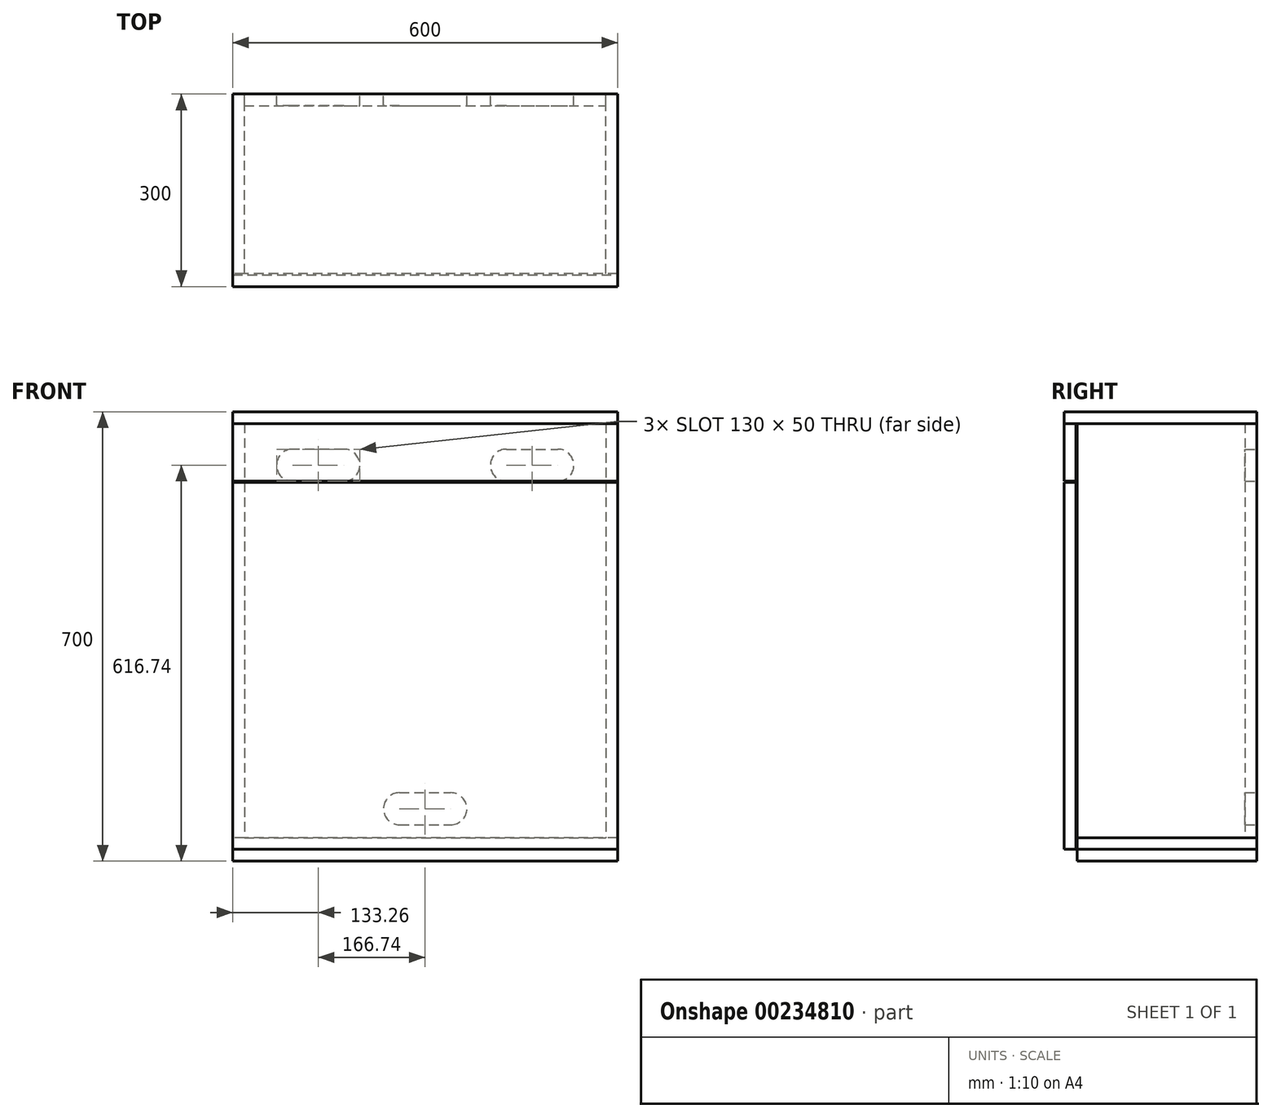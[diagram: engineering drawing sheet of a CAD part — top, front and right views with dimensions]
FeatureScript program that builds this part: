
annotation { "Feature Type Name" : "Feature", "Feature Type Description" : "" }
export const myFeature = defineFeature(function(context is Context, id is Id, definition is map)
    precondition{}
    {
        {
            var Q0;
            Q0=qCreatedBy(makeId("Top.planeOp"),FACE);
            var sketch = newSketch(context, id + "F0", { "sketchPlane" : qUnion([Q0])});
            skLineSegment(sketch, "E0.bottom", {"start": v(300, 139.87) * mm, "end": v(-300, 139.87) * mm});
            skLineSegment(sketch, "E0.top", {"start": v(300, -139.87) * mm, "end": v(-300, -139.87) * mm});
            skLineSegment(sketch, "E0.left", {"start": v(300, 139.87) * mm, "end": v(300, -139.87) * mm});
            skLineSegment(sketch, "E0.right", {"start": v(-300, 139.87) * mm, "end": v(-300, -139.87) * mm});
            skPoint(sketch, "E0.middle", {"position": v(0, 0) * mm});
            skSolve(sketch);
        }
        {
            var Q0;
            Q0=makeQuery(id+"F0.imprint","IMPRINT",FACE,{"disambiguationData":[TD([[makeQuery(id+"F0.imprint","IMPRINT",EDGE,{"derivedFrom":sQuery(id+"F0.wireOp",EDGE,"E0.bottom")}),1.0]])]});
            extrude(context, id + "F1", {"entities" : qUnion([Q0]), "depth" : 18.26 * mm, "offsetDistance" : 25 * mm});
        }
        {
            var Q0;
            Q0=makeQuery(id+"F1.opExtrude","CAP_FACE",FACE,{"disambiguationData":[OSD([sQuery(id+"F0.wireOp",EDGE,"E0.bottom"),sQuery(id+"F0.wireOp",EDGE,"E0.top"),sQuery(id+"F0.wireOp",EDGE,"E0.left"),sQuery(id+"F0.wireOp",EDGE,"E0.right")])],"isStart":false});
            var sketch = newSketch(context, id + "F2", { "sketchPlane" : qUnion([Q0])});
            skLineSegment(sketch, "E1.bottom", {"start": v(-300, -139.87) * mm, "end": v(-281.74, -139.87) * mm});
            skLineSegment(sketch, "E1.top", {"start": v(-300, 139.87) * mm, "end": v(-281.74, 139.87) * mm});
            skLineSegment(sketch, "E1.left", {"start": v(-300, -139.87) * mm, "end": v(-300, 139.87) * mm});
            skLineSegment(sketch, "E1.right", {"start": v(-281.74, -139.87) * mm, "end": v(-281.74, 139.87) * mm});
            skLineSegment(sketch, "E2.bottom", {"start": v(300, -139.87) * mm, "end": v(281.74, -139.87) * mm});
            skLineSegment(sketch, "E2.top", {"start": v(300, 139.87) * mm, "end": v(281.74, 139.87) * mm});
            skLineSegment(sketch, "E2.left", {"start": v(300, -139.87) * mm, "end": v(300, 139.87) * mm});
            skLineSegment(sketch, "E2.right", {"start": v(281.74, -139.87) * mm, "end": v(281.74, 139.87) * mm});
            skLineSegment(sketch, "E3.bottom", {"start": v(-281.74, 139.87) * mm, "end": v(281.74, 139.87) * mm});
            skLineSegment(sketch, "E3.top", {"start": v(-281.74, 121.61) * mm, "end": v(281.74, 121.61) * mm});
            skLineSegment(sketch, "E3.left", {"start": v(-281.74, 139.87) * mm, "end": v(-281.74, 121.61) * mm});
            skLineSegment(sketch, "E3.right", {"start": v(281.74, 139.87) * mm, "end": v(281.74, 121.61) * mm});
            skSolve(sketch);
        }
        {
            var Q0;
            Q0=makeQuery(id+"F2.imprint","IMPRINT",FACE,{"disambiguationData":[TD([[makeQuery(id+"F2.imprint","IMPRINT",EDGE,{"derivedFrom":sQuery(id+"F2.wireOp",EDGE,"E2.bottom")}),-1.0]])]});
            extrude(context, id + "F3", {"entities" : qUnion([Q0]), "depth" : 645.22 * mm, "offsetDistance" : 25 * mm});
        }
        {
            var Q0;
            Q0=makeQuery(id+"F2.imprint","IMPRINT",FACE,{"disambiguationData":[TD([[makeQuery(id+"F2.imprint","IMPRINT",EDGE,{"derivedFrom":sQuery(id+"F2.wireOp",EDGE,"E3.bottom")}),1.0]])]});
            var Q1;
            Q1=makeQuery(id+"F3.opExtrude","CAP_FACE",FACE,{"disambiguationData":[OSD([sQuery(id+"F2.wireOp",EDGE,"E2.bottom"),sQuery(id+"F2.wireOp",EDGE,"E2.top"),sQuery(id+"F2.wireOp",EDGE,"E2.left"),sQuery(id+"F2.wireOp",EDGE,"E2.right"),sQuery(id+"F2.wireOp",EDGE,"E3.right")])],"isStart":false});
            extrude(context, id + "F4", {"entities" : qUnion([Q0]), "endBound" : BoundingType.UP_TO_SURFACE, "endBoundEntityFace" : qUnion([Q1]), "depth" : 25 * mm});
        }
        {
            var Q0;
            Q0=makeQuery(id+"F2.imprint","IMPRINT",FACE,{"disambiguationData":[TD([[makeQuery(id+"F2.imprint","IMPRINT",EDGE,{"derivedFrom":sQuery(id+"F2.wireOp",EDGE,"E1.bottom")}),-1.0]])]});
            var Q1;
            Q1=makeQuery(id+"F4.opExtrude","CAP_FACE",FACE,{"disambiguationData":[OSD([sQuery(id+"F2.wireOp",EDGE,"E3.bottom"),sQuery(id+"F2.wireOp",EDGE,"E3.top"),sQuery(id+"F2.wireOp",EDGE,"E3.left"),sQuery(id+"F2.wireOp",EDGE,"E3.right")])],"isStart":false});
            extrude(context, id + "F5", {"entities" : qUnion([Q0]), "endBound" : BoundingType.UP_TO_SURFACE, "endBoundEntityFace" : qUnion([Q1]), "depth" : 25 * mm});
        }
        {
            var Q0;
            Q0=makeQuery(id+"F5.opExtrude","CAP_FACE",FACE,{"disambiguationData":[OSD([sQuery(id+"F2.wireOp",EDGE,"E1.bottom"),sQuery(id+"F2.wireOp",EDGE,"E1.top"),sQuery(id+"F2.wireOp",EDGE,"E1.left"),sQuery(id+"F2.wireOp",EDGE,"E1.right"),sQuery(id+"F2.wireOp",EDGE,"E3.left")])],"isStart":false});
            var sketch = newSketch(context, id + "F6", { "sketchPlane" : qUnion([Q0])});
            skLineSegment(sketch, "E4.bottom", {"start": v(-300, 139.87) * mm, "end": v(300, 139.87) * mm});
            skLineSegment(sketch, "E4.top", {"start": v(-300, -160.13) * mm, "end": v(300, -160.13) * mm});
            skLineSegment(sketch, "E4.left", {"start": v(-300, 139.87) * mm, "end": v(-300, -160.13) * mm});
            skLineSegment(sketch, "E4.right", {"start": v(300, 139.87) * mm, "end": v(300, -160.13) * mm});
            skSolve(sketch);
        }
        {
            var Q0;
            Q0 = qSketchRegion(id + "F6", true);
            extrude(context, id + "F7", {"entities" : qUnion([Q0]), "depth" : 18.26 * mm});
        }
        {
            var Q0;
            Q0=makeQuery(id+"F1.opExtrude","CAP_FACE",FACE,{"disambiguationData":[OSD([sQuery(id+"F0.wireOp",EDGE,"E0.bottom"),sQuery(id+"F0.wireOp",EDGE,"E0.top"),sQuery(id+"F0.wireOp",EDGE,"E0.left"),sQuery(id+"F0.wireOp",EDGE,"E0.right")])],"isStart":true});
            extrude(context, id + "F8", {"entities" : qUnion([Q0]), "depth" : 18.26 * mm});
        }
        {
            var Q0;
            Q0=makeQuery(id+"F4.opExtrude","SWEPT_FACE",FACE,{"disambiguationData":[OSD([sQuery(id+"F2.wireOp",EDGE,"E3.bottom")])]});
            var sketch = newSketch(context, id + "F9", { "sketchPlane" : qUnion([Q0])});
            skLineSegment(sketch, "E5", {"start": v(0, 0) * mm, "end": v(0, 663.48) * mm, "construction": true});
            skCircle(sketch, "E6", {"center": v(126.74, 598.48) * mm, "radius": 25 * mm});
            skCircle(sketch, "E7.MirrorC", {"center": v(206.74, 598.48) * mm, "radius": 25 * mm});
            skLineSegment(sketch, "E8", {"start": v(126.74, 623.48) * mm, "end": v(206.74, 623.48) * mm});
            skLineSegment(sketch, "E9", {"start": v(126.74, 573.48) * mm, "end": v(206.74, 573.48) * mm});
            skCircle(sketch, "E10.MirrorC", {"center": v(-126.74, 598.48) * mm, "radius": 25 * mm});
            skCircle(sketch, "E11.MirrorC", {"center": v(-206.74, 598.48) * mm, "radius": 25 * mm});
            skLineSegment(sketch, "E12.MirrorCS", {"start": v(-126.74, 623.48) * mm, "end": v(-206.74, 623.48) * mm});
            skLineSegment(sketch, "E13.MirrorCS", {"start": v(-126.74, 573.48) * mm, "end": v(-206.74, 573.48) * mm});
            skCircle(sketch, "E14.MirrorC", {"center": v(40, 63.26) * mm, "radius": 25 * mm});
            skCircle(sketch, "E15.MirrorC", {"center": v(-40, 63.26) * mm, "radius": 25 * mm});
            skLineSegment(sketch, "E16.MirrorCS", {"start": v(40, 88.26) * mm, "end": v(-40, 88.26) * mm});
            skLineSegment(sketch, "E17.MirrorCS", {"start": v(40, 38.26) * mm, "end": v(-40, 38.26) * mm});
            skSolve(sketch);
        }
        {
            var Q0;
            Q0 = qSketchRegion(id + "F9", true);
            extrude(context, id + "F10", {"entities" : qUnion([Q0]), "operationType" : NewBodyOperationType.REMOVE, "oppositeDirection" : true, "depth" : 25 * mm});
        }
        {
            var Q0;
            Q0=makeQuery(id+"F7.opExtrude","SWEPT_FACE",FACE,{"disambiguationData":[OSD([sQuery(id+"F6.wireOp",EDGE,"E4.top")])]});
            var sketch = newSketch(context, id + "F11", { "sketchPlane" : qUnion([Q0])});
            skLineSegment(sketch, "E18.bottom", {"start": v(-300, 663.48) * mm, "end": v(300, 663.48) * mm});
            skLineSegment(sketch, "E18.top", {"start": v(-300, 573.48) * mm, "end": v(300, 573.48) * mm});
            skLineSegment(sketch, "E18.left", {"start": v(-300, 663.48) * mm, "end": v(-300, 573.48) * mm});
            skLineSegment(sketch, "E18.right", {"start": v(300, 663.48) * mm, "end": v(300, 573.48) * mm});
            skSolve(sketch);
        }
        {
            var Q0;
            Q0 = qSketchRegion(id + "F11", true);
            extrude(context, id + "F12", {"entities" : qUnion([Q0]), "oppositeDirection" : true, "depth" : 18.26 * mm});
        }
        {
            var Q0;
            Q0=makeQuery(id+"F12.opExtrude","CAP_FACE",FACE,{"disambiguationData":[OSD([sQuery(id+"F11.wireOp",EDGE,"E18.bottom"),sQuery(id+"F11.wireOp",EDGE,"E18.top"),sQuery(id+"F11.wireOp",EDGE,"E18.left"),sQuery(id+"F11.wireOp",EDGE,"E18.right")])],"isStart":true});
            var sketch = newSketch(context, id + "F13", { "sketchPlane" : qUnion([Q0])});
            skLineSegment(sketch, "E19.bottom", {"start": v(-300, 571.48) * mm, "end": v(300, 571.48) * mm});
            skLineSegment(sketch, "E19.top", {"start": v(-300, 0) * mm, "end": v(300, 0) * mm});
            skLineSegment(sketch, "E19.left", {"start": v(-300, 571.48) * mm, "end": v(-300, 0) * mm});
            skLineSegment(sketch, "E19.right", {"start": v(300, 571.48) * mm, "end": v(300, 0) * mm});
            skSolve(sketch);
        }
        {
            var Q0;
            Q0 = qSketchRegion(id + "F13", true);
            extrude(context, id + "F14", {"entities" : qUnion([Q0]), "oppositeDirection" : true, "depth" : 18.26 * mm});
        }
    });
